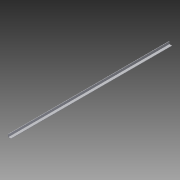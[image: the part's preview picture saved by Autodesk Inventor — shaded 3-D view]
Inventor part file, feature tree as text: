
AUTODESK INVENTOR PART (.ipt)
format: ipt  version: 2013 (Build 170138000, 138)  size: 74,240 bytes
history: native  units: in
note: dims shown in document units (in); Inventor stores cm internally (conversion verified against a paired STEP export)
features: extrude x1, sketch x1
ambient origin geometry x8: Origin, YZ Plane, XZ Plane, XY Plane, X Axis, Y Axis, Z Axis, Center Point
bodies: Solid1 (feature_tree)
feature tree (2):
  extrude  "Extrusion1"  Depth=0.0625in
  sketch  "Sketch1"  dims[d0=0.5in d1=0.0625in d2=0.5in d3=0.0625in d4=28.375in d5=0.0in]
